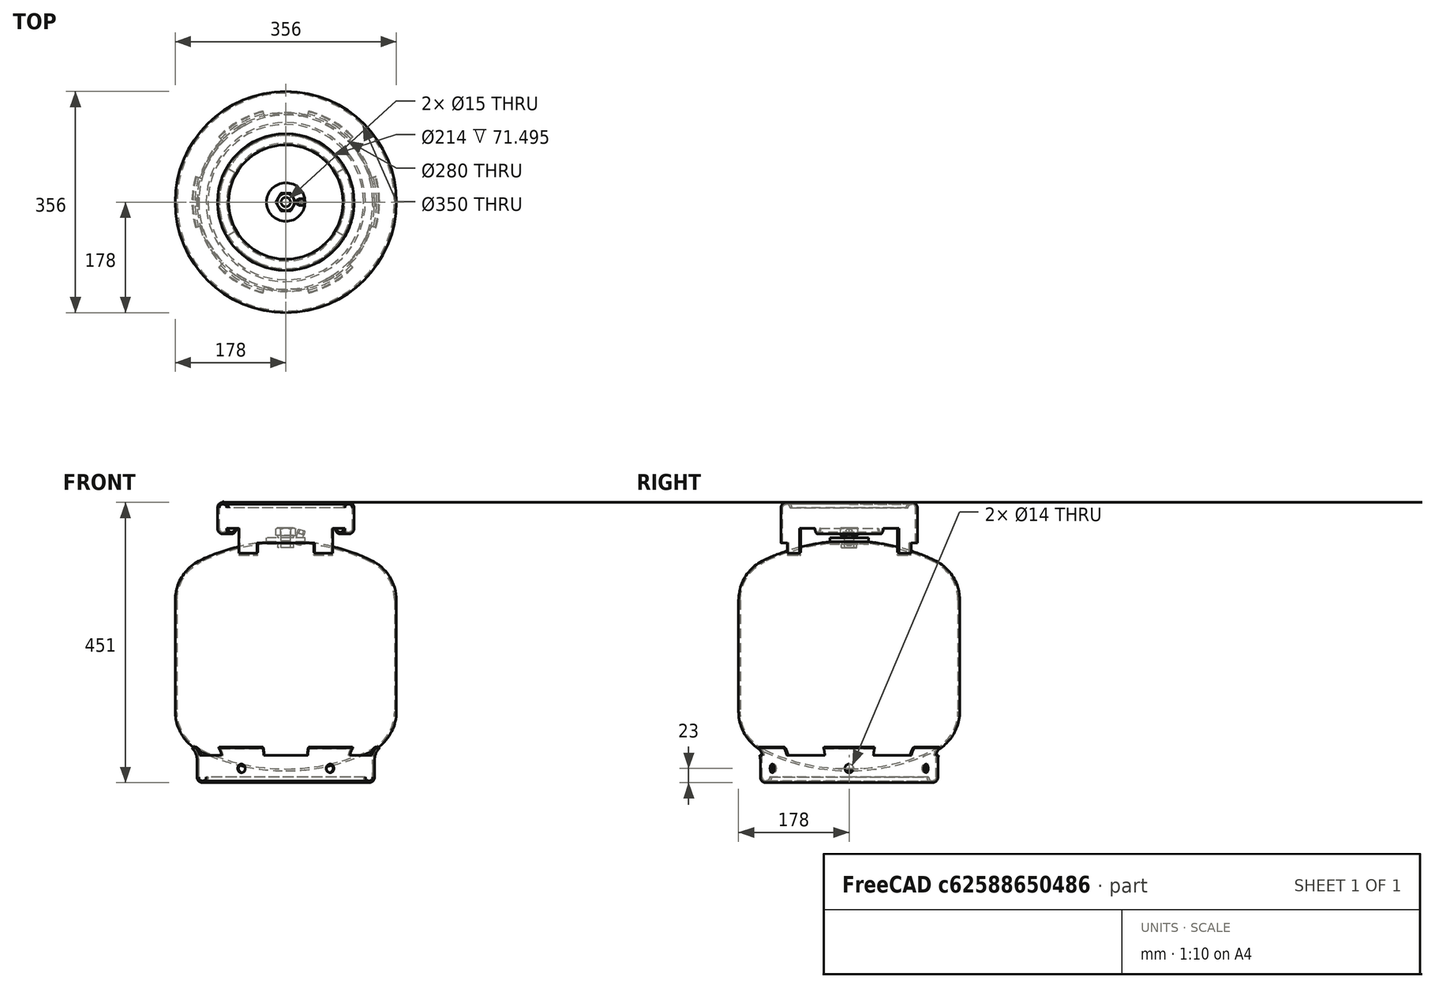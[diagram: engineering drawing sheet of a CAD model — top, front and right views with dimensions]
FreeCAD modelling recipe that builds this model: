
FCSTD DOCUMENT  (FreeCAD 0.18R13516 (Git))
Label: BOTIJÃO GAS - CJ
License: All rights reserved
LicenseURL: http://en.wikipedia.org/wiki/All_rights_reserved
objects: Part::FeaturePython×6, Part::MultiFuse×2, Part::Cut×2
note: 10 computed .brp shape members not serialized (recipe doc carries the construction recipe); baked Part::Feature solids carry a one-line shape summary decoded from their .brp

FEATURE [Part::FeaturePython] import_01  label="BOTIJÃO - 1_01"  # a2plus imported part (geometry in sourceFile) (typed FeaturePython)
  fixedPosition = true
  sourceFile = <userpath>/RSRV/FREECAD/40-BOTIJÃO DE GAS - GAS CANISTER/BOTIJÃO - 1.fcstd
  timeLastImport = 1.52461e+09
  updateColors = true
FEATURE [Part::FeaturePython] import_02  label="BOTIJÃO - 2_01"  # a2plus imported part (geometry in sourceFile) (typed FeaturePython)
  Placement = pos=(0,0,162) rot=(1,0,0;1.5708rad)
  fixedPosition = false
  sourceFile = <userpath>/RSRV/FREECAD/40-BOTIJÃO DE GAS - GAS CANISTER/BOTIJÃO - 2.fcstd
  timeLastImport = 1.5246e+09
  updateColors = true
FEATURE [Part::FeaturePython] import_03  label="BOTIJÃO - 3_01"  # a2plus imported part (geometry in sourceFile) (typed FeaturePython)
  Placement = pos=(0,0,-195) rot=(0,0,1;0rad)
  fixedPosition = false
  sourceFile = <userpath>/RSRV/FREECAD/40-BOTIJÃO DE GAS - GAS CANISTER/BOTIJÃO - 3.fcstd
  timeLastImport = 1.52461e+09
  updateColors = true
FEATURE [Part::FeaturePython] import_04  label="BOTIJÃO - 4_01"  # a2plus imported part (geometry in sourceFile) (typed FeaturePython)
  Placement = pos=(0,0,180) rot=(0,0,1;0rad)
  fixedPosition = false
  sourceFile = <userpath>/RSRV/FREECAD/40-BOTIJÃO DE GAS - GAS CANISTER/BOTIJÃO - 4.fcstd
  timeLastImport = 1.52461e+09
  updateColors = true
FEATURE [Part::FeaturePython] import_05  label="BOTIJÃO - 5-1_01"  # a2plus imported part (geometry in sourceFile) (typed FeaturePython)
  Placement = pos=(0,0,174) rot=(0,0,1;0rad)
  fixedPosition = false
  sourceFile = <userpath>/RSRV/FREECAD/40-BOTIJÃO DE GAS - GAS CANISTER/BOTIJÃO - 5-1.fcstd
  timeLastImport = 1.52461e+09
  updateColors = true
FEATURE [Part::FeaturePython] import_06  label="BOTIJÃO - 6_01"  # a2plus imported part (geometry in sourceFile) (typed FeaturePython)
  Placement = pos=(24.0872,0,196.067) rot=(0,1,0;0.261799rad)
  fixedPosition = false
  sourceFile = <userpath>/RSRV/FREECAD/40-BOTIJÃO DE GAS - GAS CANISTER/BOTIJÃO - 6.fcstd
  timeLastImport = 1.52461e+09
  updateColors = true
FEATURE [Part::MultiFuse] Fusion
  Shapes = -> [import_01,import_02,import_03]
FEATURE [Part::Cut] Cut
  Base = -> Fusion
  Tool = -> import_04
FEATURE [Part::Cut] Cut001
  Base = -> import_04
  Tool = -> import_06
FEATURE [Part::MultiFuse] Fusion001
  Shapes = -> [import_06,Cut001,Cut,import_05]
